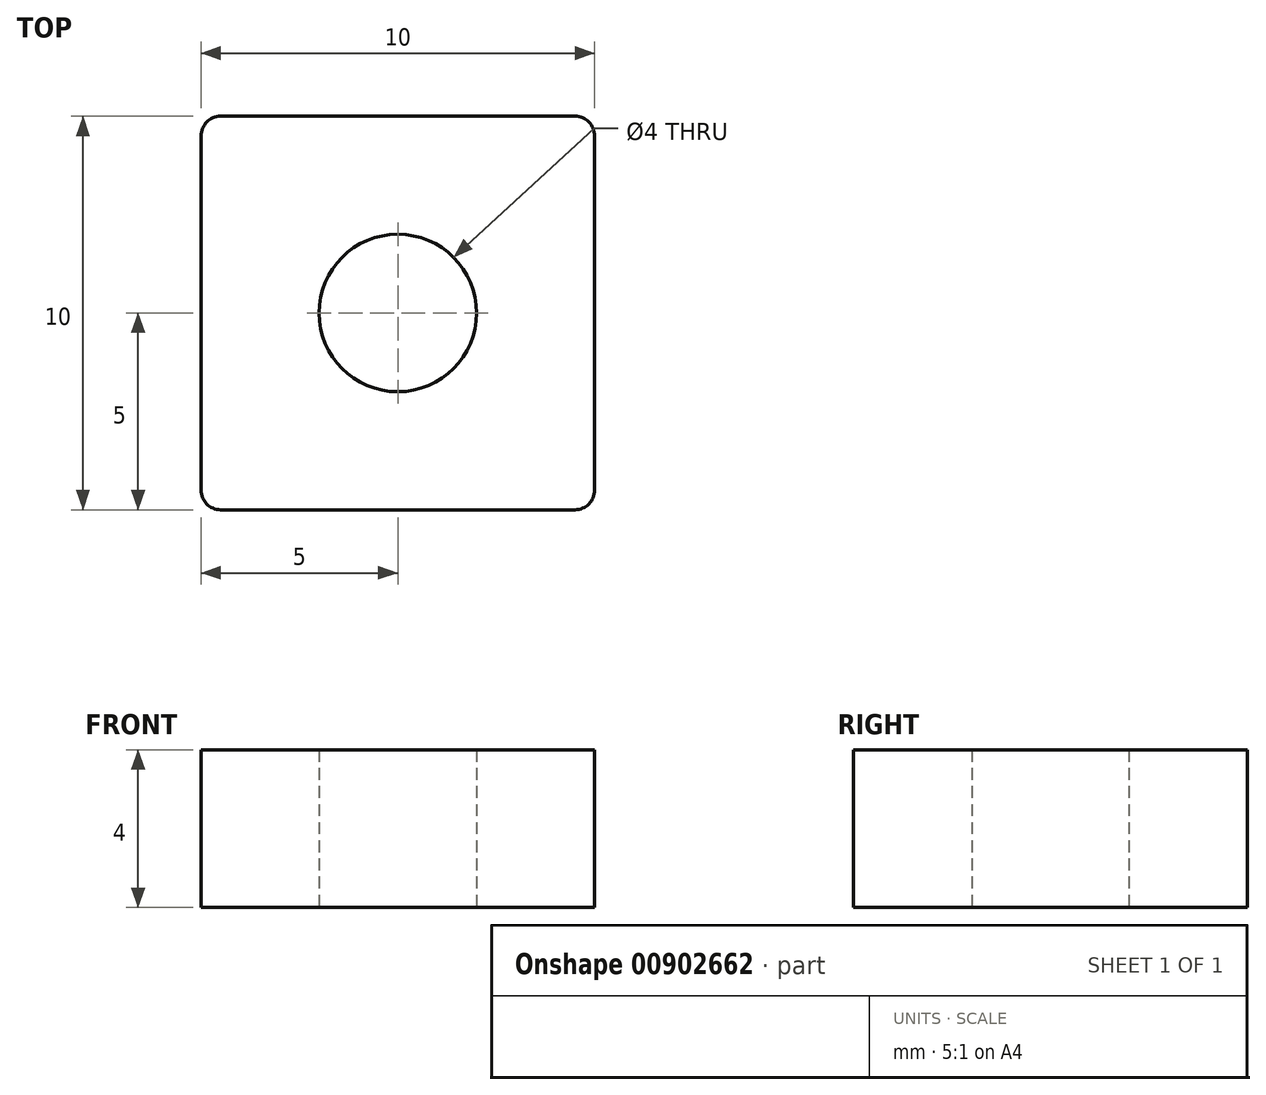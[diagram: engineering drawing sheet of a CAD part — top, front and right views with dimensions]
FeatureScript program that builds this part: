
annotation { "Feature Type Name" : "Feature", "Feature Type Description" : "" }
export const myFeature = defineFeature(function(context is Context, id is Id, definition is map)
    precondition{}
    {
        {
            var Q0;
            Q0=qCreatedBy(makeId("Top.planeOp"),FACE);
            var sketch = newSketch(context, id + "F0", { "sketchPlane" : qUnion([Q0])});
            skLineSegment(sketch, "E0.bottom", {"start": v(4.5, -5) * mm, "end": v(-4.5, -5) * mm});
            skLineSegment(sketch, "E0.top", {"start": v(4.5, 5) * mm, "end": v(-4.5, 5) * mm});
            skLineSegment(sketch, "E0.left", {"start": v(5, -4.5) * mm, "end": v(5, 4.5) * mm});
            skLineSegment(sketch, "E0.right", {"start": v(-5, -4.5) * mm, "end": v(-5, 4.5) * mm});
            skPoint(sketch, "E0.middle", {"position": v(0, 0) * mm});
            skCircle(sketch, "E1", {"center": v(0, 0) * mm, "radius": 2 * mm});
            skPoint(sketch, "E2.visualSharp", {"position": v(-5, 5) * mm});
            skArc(sketch, "E2.filletArc", {"start": v(-4.5, 5) * mm, "mid": v(-4.85, 4.85) * mm, "end": v(-5, 4.5) * mm});
            skPoint(sketch, "E3.visualSharp", {"position": v(5, 5) * mm});
            skArc(sketch, "E3.filletArc", {"start": v(5, 4.5) * mm, "mid": v(4.85, 4.85) * mm, "end": v(4.5, 5) * mm});
            skPoint(sketch, "E4.visualSharp", {"position": v(5, -5) * mm});
            skArc(sketch, "E4.filletArc", {"start": v(4.5, -5) * mm, "mid": v(4.85, -4.85) * mm, "end": v(5, -4.5) * mm});
            skPoint(sketch, "E5.visualSharp", {"position": v(-5, -5) * mm});
            skArc(sketch, "E5.filletArc", {"start": v(-5, -4.5) * mm, "mid": v(-4.85, -4.85) * mm, "end": v(-4.5, -5) * mm});
            skSolve(sketch);
        }
        {
            var Q0;
            Q0 = qSketchRegion(id + "F0", true);
            extrude(context, id + "F1", {"entities" : qUnion([Q0]), "depth" : 4 * mm, "offsetDistance" : 25 * mm});
        }
    });
